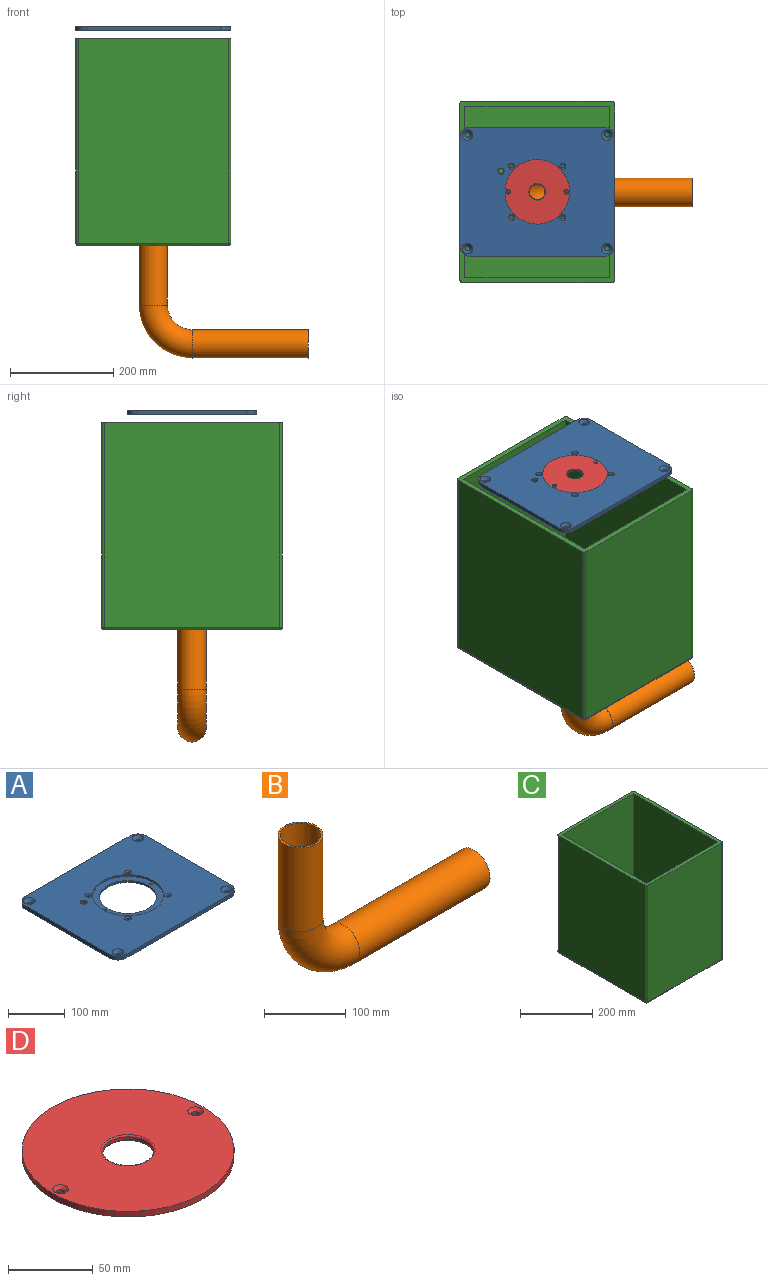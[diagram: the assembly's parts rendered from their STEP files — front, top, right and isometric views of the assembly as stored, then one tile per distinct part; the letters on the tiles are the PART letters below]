
ASSEMBLY  parts=4 mates=3
PART A: 34 faces, bbox 300x250x8 mm
  f0: plane 125x125mm, normal (0,0,1), area 4378.6mm2, adj f8,f13,f14,f22
  f1: plane 260x8mm, normal (0,1,0), area 2080mm2, adj f2,f20,f21,f23
  f2: cylinder r=20mm len=20mm, axis (0,0,-1), area 251.3mm2, adj f1,f3,f21,f23
  f3: plane 210x8mm, normal (-1,0,0), area 1680mm2, adj f2,f4,f21,f23
  f4: cylinder r=20mm len=20mm, axis (0,0,-1), area 251.3mm2, adj f3,f5,f21,f23
  f5: plane 260x8mm, normal (0,-1,0), area 2080mm2, adj f4,f6,f21,f23
  f6: cylinder r=20mm len=20mm, axis (0,0,-1), area 251.3mm2, adj f5,f7,f21,f23
  f7: plane 210x8mm, normal (1,0,0), area 1680mm2, adj f6,f20,f21,f23
  f8: cylinder r=50mm len=100mm, axis (0,0,-1), area 1256.6mm2, adj f0,f21
  f9: cylinder r=4.2mm len=8.4mm, axis (0,0,-1), area 52.8mm2, adj f21,f26
  f10: cylinder r=4.2mm len=8.4mm, axis (0,0,-1), area 52.8mm2, adj f21,f25
  f11: cylinder r=4.2mm len=8.4mm, axis (0,0,-1), area 52.8mm2, adj f21,f27
  f12: cylinder r=4.2mm len=8.4mm, axis (0,0,-1), area 52.8mm2, adj f21,f24
  f13: cylinder r=2.5mm len=5mm, axis (0,0,-1), area 62.8mm2, adj f0,f21
  f14: cylinder r=2.5mm len=5mm, axis (0,0,-1), area 62.8mm2, adj f0,f21
  f15: cylinder r=3mm len=6mm, axis (0,0,-1), area 94.2mm2, adj f21,f30
  f16: cylinder r=3mm len=6mm, axis (0,0,-1), area 94.2mm2, adj f21,f29
  f17: cylinder r=3mm len=6mm, axis (0,0,-1), area 94.2mm2, adj f21,f28
  f18: cylinder r=3mm len=6mm, axis (0,0,-1), area 94.2mm2, adj f21,f31
  f19: cylinder r=5mm len=10mm, axis (0,0,-1), area 188.5mm2, adj f32,f33
  f20: cylinder r=20mm len=20mm, axis (0,0,-1), area 251.3mm2, adj f1,f7,f21,f23
  f21: plane 300x250mm, normal (0,0,-1), area 66315.5mm2, adj f1,f2,f3,f4,f5,f6,f7,f8
  f22: cylinder r=62.5mm len=125mm, axis (0,0,-1), area 1570.8mm2, adj f0,f23
  f23: plane 300x250mm, normal (0,0,1), area 60511.9mm2, adj f1,f2,f3,f4,f5,f6,f7,f20
  f24: cone r=4.2mm half-angle=45deg, axis (0,0,1), area 383.9mm2, adj f12,f23
  f25: cone r=4.2mm half-angle=45deg, axis (0,0,1), area 383.9mm2, adj f10,f23
  f26: cone r=4.2mm half-angle=45deg, axis (0,0,1), area 383.9mm2, adj f9,f23
  f27: cone r=4.2mm half-angle=45deg, axis (0,0,1), area 383.9mm2, adj f11,f23
  f28: cone r=3mm half-angle=45deg, axis (0,0,1), area 120mm2, adj f17,f23
  f29: cone r=3mm half-angle=45deg, axis (0,0,1), area 120mm2, adj f16,f23
  f30: cone r=3mm half-angle=45deg, axis (0,0,1), area 120mm2, adj f15,f23
  f31: cone r=3mm half-angle=45deg, axis (0,0,1), area 120mm2, adj f18,f23
  f32: torus R=6mm, axis (0,0,1), area 52.9mm2, adj f19,f23
  f33: torus R=6mm, axis (0,0,1), area 52.9mm2, adj f19,f21
PART B: 8 faces, bbox 335.9x55x235.9 mm
  f0: cylinder r=25mm len=125mm, axis (0,0,-1), area 19635mm2, adj f1,f3
  f1: torus R=75mm, axis (0,-1,0), area 18505.5mm2, adj f0,f2
  f2: cylinder r=25mm len=225mm, axis (1,0,0), area 35342.9mm2, adj f1,f4
  f3: plane 55x55mm, normal (0,0,1), area 412.3mm2, adj f0,f5
  f4: plane 55x55mm, normal (1,0,0), area 412.3mm2, adj f2,f7
  f5: cylinder r=27.5mm len=125mm, axis (0,0,-1), area 21598.4mm2, adj f3,f6
  f6: torus R=75mm, axis (0,-1,0), area 20356.1mm2, adj f5,f7
  f7: cylinder r=27.5mm len=225mm, axis (1,0,0), area 38877.2mm2, adj f4,f6
PART C: 24 faces, bbox 300x350x400 mm
  f0: plane 350x300mm, normal (0,0,1), area 12578.5mm2, adj f1,f2,f3,f4,f6,f7,f8,f9
  f1: plane 395x290mm, normal (0,1,0), area 114550mm2, adj f0,f16,f20,f22
  f2: plane 395x340mm, normal (-1,0,0), area 134300mm2, adj f0,f13,f19,f22
  f3: plane 395x290mm, normal (0,-1,0), area 114550mm2, adj f0,f11,f13,f14
  f4: plane 395x340mm, normal (1,0,0), area 134300mm2, adj f0,f11,f15,f16
  f5: plane 340x290mm, normal (0,0,-1), area 96636.5mm2, adj f14,f15,f19,f20,f23
  f6: plane 390x280mm, normal (0,-1,0), area 109200mm2, adj f0,f7,f9,f10
  f7: plane 390x330mm, normal (1,0,0), area 128700mm2, adj f0,f6,f8,f10
  f8: plane 390x280mm, normal (0,1,0), area 109200mm2, adj f0,f7,f9,f10
  f9: plane 390x330mm, normal (-1,0,0), area 128700mm2, adj f0,f6,f8,f10
  f10: plane 330x280mm, normal (0,0,1), area 90436.5mm2, adj f6,f7,f8,f9,f23
  f11: cylinder r=5mm len=395mm, axis (0,0,1), area 3102.3mm2, adj f0,f3,f4,f12
  f12: sphere r=5mm, area 39.3mm2, adj f11,f14,f15
  f13: cylinder r=5mm len=395mm, axis (0,0,-1), area 3102.3mm2, adj f0,f2,f3,f17
  f14: cylinder r=5mm len=290mm, axis (1,0,0), area 2277.7mm2, adj f3,f5,f12,f17
  f15: cylinder r=5mm len=340mm, axis (0,1,0), area 2670.4mm2, adj f4,f5,f12,f18
  f16: cylinder r=5mm len=395mm, axis (0,0,-1), area 3102.3mm2, adj f0,f1,f4,f18
  f17: sphere r=5mm, area 39.3mm2, adj f13,f14,f19
  f18: sphere r=5mm, area 39.3mm2, adj f15,f16,f20
  f19: cylinder r=5mm len=340mm, axis (0,-1,0), area 2670.4mm2, adj f2,f5,f17,f21
  f20: cylinder r=5mm len=290mm, axis (-1,0,0), area 2277.7mm2, adj f1,f5,f18,f21
  f21: sphere r=5mm, area 39.3mm2, adj f19,f20,f22
  f22: cylinder r=5mm len=395mm, axis (0,0,1), area 3102.3mm2, adj f0,f1,f2,f21
  f23: cylinder r=25mm len=50mm, axis (0,0,-1), area 1570.8mm2, adj f5,f10
PART D: 10 faces, bbox 125x125x4 mm
  f0: cylinder r=15mm len=30mm, axis (0,0,1), area 188.5mm2, adj f8,f9
  f1: cylinder r=2.5mm len=5mm, axis (0,0,1), area 31.4mm2, adj f4,f7
  f2: cylinder r=2.5mm len=5mm, axis (0,0,1), area 31.4mm2, adj f4,f6
  f3: cylinder r=62.5mm len=125mm, axis (0,0,1), area 1570.8mm2, adj f4,f5
  f4: plane 125x125mm, normal (0,0,-1), area 11428.3mm2, adj f1,f2,f3,f9
  f5: plane 125x125mm, normal (0,0,1), area 11340.4mm2, adj f3,f6,f7,f8
  f6: cone r=2.5mm half-angle=45deg, axis (0,0,1), area 62.2mm2, adj f2,f5
  f7: cone r=2.5mm half-angle=45deg, axis (0,0,1), area 62.2mm2, adj f1,f5
  f8: torus R=16mm, axis (0,0,1), area 151.6mm2, adj f0,f5
  f9: torus R=16mm, axis (0,0,1), area 151.6mm2, adj f0,f4
PLACE A t=(-97.35,-32.69,27.27)mm
PLACE B t=(-97.35,-32.69,-379.73)mm
PLACE C t=(-97.35,-32.69,-389.73)mm
PLACE D t=(-97.35,-32.69,35.27)mm
MATE fastened C.f23 <-> A.f22  axis (0,0,1) through (-97.35,-32.69,-379.73)mm
MATE fastened B.f5 <-> C.f23  axis (0,0,1) through (-97.35,-32.69,-379.73)mm
MATE fastened A.f22 <-> D.f3  axis (0,0,1) through (-97.35,-32.69,35.27)mm
